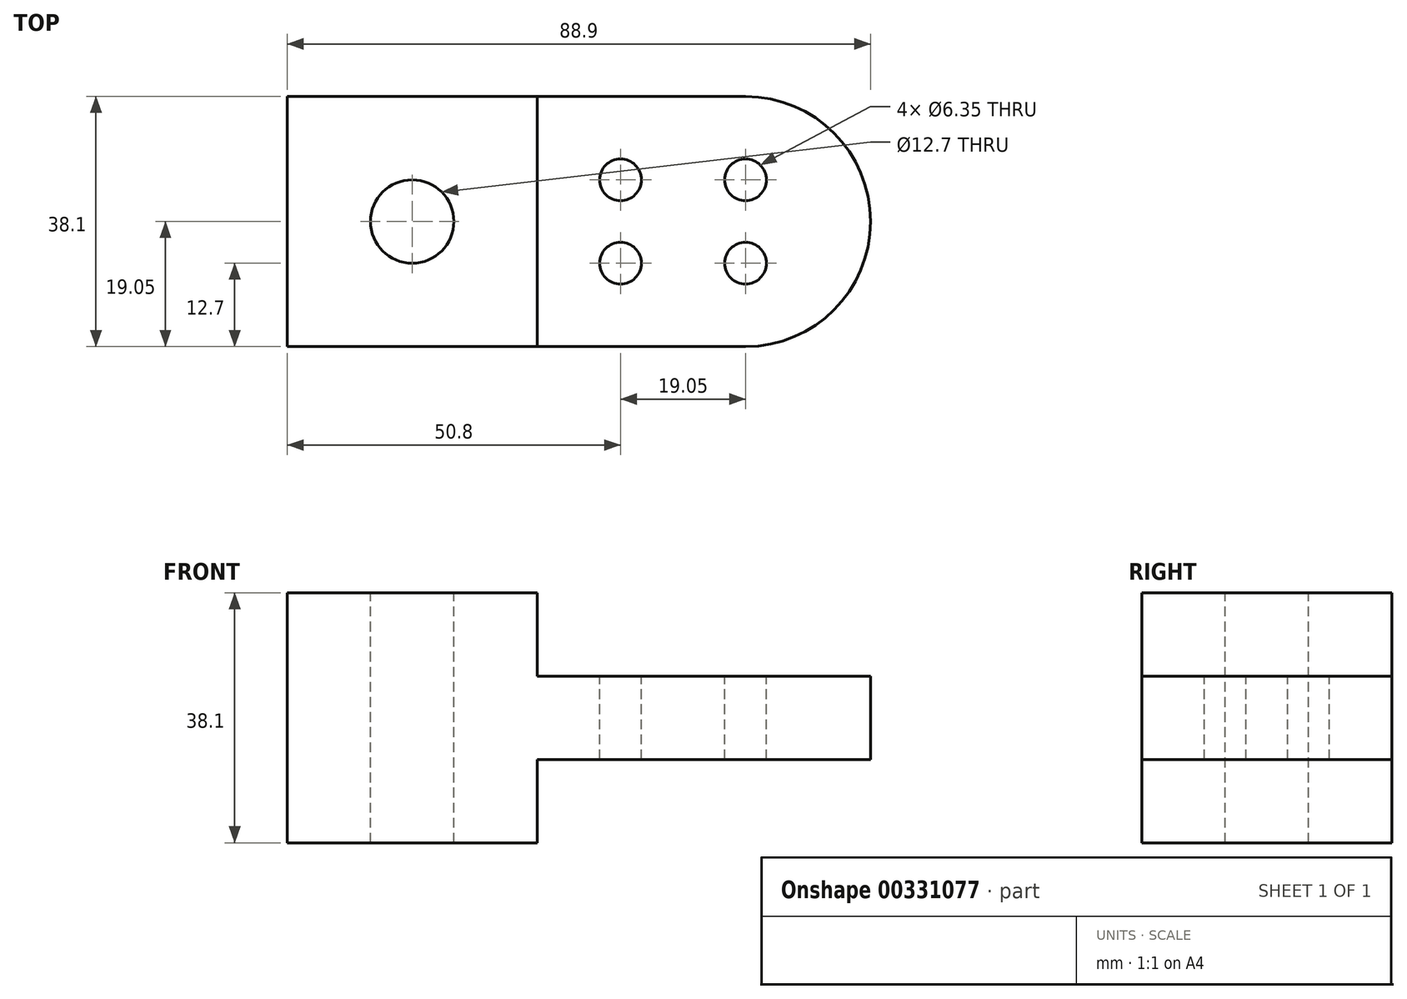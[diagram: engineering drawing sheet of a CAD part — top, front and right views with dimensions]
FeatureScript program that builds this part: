
annotation { "Feature Type Name" : "Feature", "Feature Type Description" : "" }
export const myFeature = defineFeature(function(context is Context, id is Id, definition is map)
    precondition{}
    {
        {
            var Q0;
            Q0=qCreatedBy(makeId("Front.planeOp"),FACE);
            var sketch = newSketch(context, id + "F0", { "sketchPlane" : qUnion([Q0])});
            skLineSegment(sketch, "E0.bottom", {"start": v(0, 0) * mm, "end": v(38.1, 0) * mm});
            skLineSegment(sketch, "E0.top", {"start": v(0, 38.1) * mm, "end": v(38.1, 38.1) * mm});
            skLineSegment(sketch, "E0.left", {"start": v(0, 0) * mm, "end": v(0, 38.1) * mm});
            skLineSegment(sketch, "E0.right", {"start": v(69.85, 12.7) * mm, "end": v(69.85, 25.4) * mm});
            skLineSegment(sketch, "E1.top", {"start": v(69.85, 25.4) * mm, "end": v(38.1, 25.4) * mm});
            skLineSegment(sketch, "E1.right", {"start": v(38.1, 38.1) * mm, "end": v(38.1, 25.4) * mm});
            skLineSegment(sketch, "E2.top", {"start": v(69.85, 12.7) * mm, "end": v(38.1, 12.7) * mm});
            skLineSegment(sketch, "E2.right", {"start": v(38.1, 0) * mm, "end": v(38.1, 12.7) * mm});
            skSolve(sketch);
        }
        {
            var Q0;
            Q0 = qSketchRegion(id + "F0", true);
            extrude(context, id + "F1", {"entities" : qUnion([Q0]), "endBound" : BoundingType.SYMMETRIC, "depth" : 38.1 * mm});
        }
        {
            var Q0;
            Q0=makeQuery(id+"F1.opExtrude","SWEPT_FACE",FACE,{"disambiguationData":[OSD([sQuery(id+"F0.wireOp",EDGE,"E1.top")])]});
            var sketch = newSketch(context, id + "F2", { "sketchPlane" : qUnion([Q0])});
            skArc(sketch, "E3", {"start": v(69.85, -19.05) * mm, "mid": v(88.9, 0) * mm, "end": v(69.85, 19.05) * mm});
            skSolve(sketch);
        }
        {
            var Q0;
            Q0 = qSketchRegion(id + "F2", true);
            var Q1;
            Q1=makeQuery(id+"F2.imprint","IMPRINT",FACE,{"disambiguationData":[TD([[makeQuery(id+"F2.imprint","IMPRINT",EDGE,{"derivedFrom":sQuery(id+"F2.wireOp",EDGE,"E3")}),1.0]])]});
            extrude(context, id + "F3", {"entities" : qUnion([Q0, Q1]), "operationType" : NewBodyOperationType.ADD, "oppositeDirection" : true, "depth" : 12.7 * mm});
        }
        {
            var Q0;
            Q0=makeQuery(id+"F1.opExtrude","SWEPT_FACE",FACE,{"disambiguationData":[OSD([sQuery(id+"F0.wireOp",EDGE,"E0.top")])]});
            var sketch = newSketch(context, id + "F4", { "sketchPlane" : qUnion([Q0])});
            skLineSegment(sketch, "E4.0.0", {"start": v(69.85, 19.05) * mm, "end": v(38.1, 19.05) * mm});
            skLineSegment(sketch, "E4.0.1", {"start": v(38.1, 19.05) * mm, "end": v(38.1, -19.05) * mm});
            skLineSegment(sketch, "E4.0.2", {"start": v(38.1, -19.05) * mm, "end": v(69.85, -19.05) * mm});
            skArc(sketch, "E4.0.3", {"start": v(69.85, -19.05) * mm, "mid": v(88.9, 0) * mm, "end": v(69.85, 19.05) * mm});
            skCircle(sketch, "E5", {"center": v(19.05, 0) * mm, "radius": 6.35 * mm});
            skCircle(sketch, "E6", {"center": v(50.8, 6.35) * mm, "radius": 3.18 * mm});
            skCircle(sketch, "E7.0.1.0", {"center": v(50.8, -6.35) * mm, "radius": 3.18 * mm});
            skCircle(sketch, "E7.1.0.0", {"center": v(69.85, 6.35) * mm, "radius": 3.18 * mm});
            skCircle(sketch, "E7.1.1.0", {"center": v(69.85, -6.35) * mm, "radius": 3.18 * mm});
            skLineSegment(sketch, "E7.direction1", {"start": v(50.8, 6.35) * mm, "end": v(69.85, 6.35) * mm, "construction": true});
            skLineSegment(sketch, "E7.direction2", {"start": v(50.8, 6.35) * mm, "end": v(50.8, -6.35) * mm, "construction": true});
            skSolve(sketch);
        }
        {
            var Q0;
            Q0=makeQuery(id+"F4.imprint","IMPRINT",FACE,{"disambiguationData":[TD([[makeQuery(id+"F4.imprint","IMPRINT",EDGE,{"derivedFrom":sQuery(id+"F4.wireOp",EDGE,"E5")}),1.0]])]});
            var Q1;
            Q1=makeQuery(id+"F4.imprint","IMPRINT",FACE,{"disambiguationData":[TD([[makeQuery(id+"F4.imprint","IMPRINT",EDGE,{"derivedFrom":sQuery(id+"F4.wireOp",EDGE,"E6")}),1.0]])]});
            var Q2;
            Q2=makeQuery(id+"F4.imprint","IMPRINT",FACE,{"disambiguationData":[TD([[makeQuery(id+"F4.imprint","IMPRINT",EDGE,{"derivedFrom":sQuery(id+"F4.wireOp",EDGE,"E7.0.1.0")}),1.0]])]});
            var Q3;
            Q3=makeQuery(id+"F4.imprint","IMPRINT",FACE,{"disambiguationData":[TD([[makeQuery(id+"F4.imprint","IMPRINT",EDGE,{"derivedFrom":sQuery(id+"F4.wireOp",EDGE,"E7.1.1.0")}),1.0]])]});
            var Q4;
            Q4=makeQuery(id+"F4.imprint","IMPRINT",FACE,{"disambiguationData":[TD([[makeQuery(id+"F4.imprint","IMPRINT",EDGE,{"derivedFrom":sQuery(id+"F4.wireOp",EDGE,"E7.1.0.0")}),1.0]])]});
            extrude(context, id + "F5", {"entities" : qUnion([Q0, Q1, Q2, Q3, Q4]), "operationType" : NewBodyOperationType.REMOVE, "endBound" : BoundingType.THROUGH_ALL, "oppositeDirection" : true, "depth" : 25.4 * mm});
        }
    });
